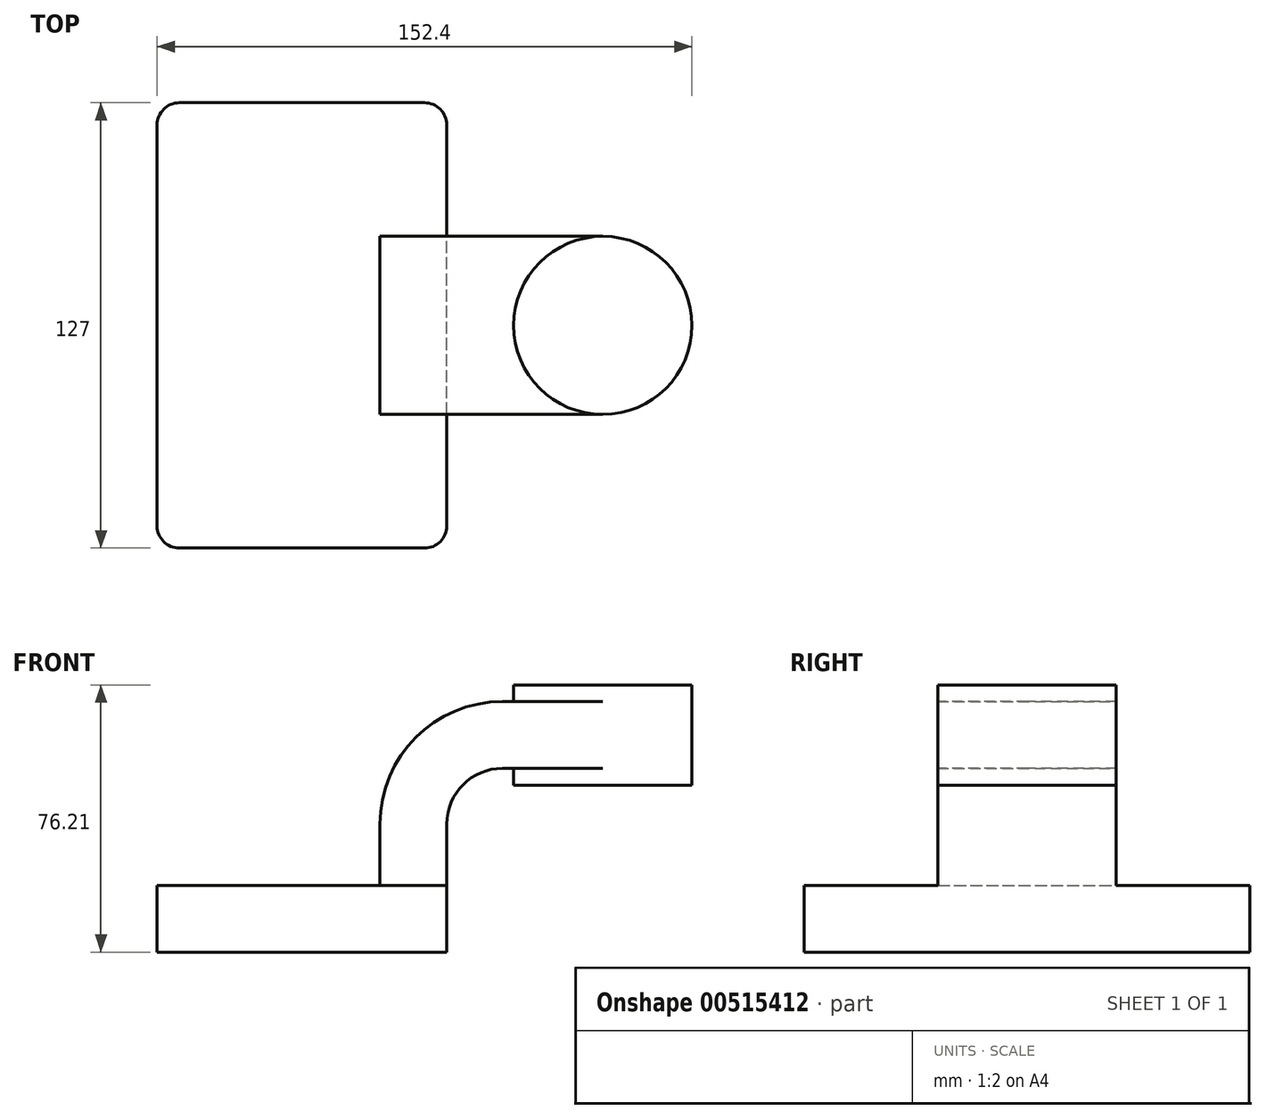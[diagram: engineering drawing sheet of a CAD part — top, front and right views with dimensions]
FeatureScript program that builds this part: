
annotation { "Feature Type Name" : "Feature", "Feature Type Description" : "" }
export const myFeature = defineFeature(function(context is Context, id is Id, definition is map)
    precondition{}
    {
        {
            var Q0;
            Q0=qCreatedBy(makeId("Front.planeOp"),FACE);
            var sketch = newSketch(context, id + "F0", { "sketchPlane" : qUnion([Q0])});
            skLineSegment(sketch, "E0.bottom", {"start": v(-41.28, 9.52) * mm, "end": v(41.28, 9.53) * mm});
            skLineSegment(sketch, "E0.top", {"start": v(-41.28, -9.53) * mm, "end": v(41.28, -9.53) * mm});
            skLineSegment(sketch, "E0.left", {"start": v(-41.28, 9.52) * mm, "end": v(-41.28, -9.53) * mm});
            skLineSegment(sketch, "E0.right", {"start": v(41.28, 9.53) * mm, "end": v(41.28, -9.52) * mm});
            skPoint(sketch, "E0.middle", {"position": v(0, 0) * mm});
            skLineSegment(sketch, "E1.bottom", {"start": v(60.32, 66.67) * mm, "end": v(111.12, 66.67) * mm});
            skLineSegment(sketch, "E1.top", {"start": v(60.32, 38.1) * mm, "end": v(111.12, 38.1) * mm});
            skLineSegment(sketch, "E1.left", {"start": v(60.32, 66.67) * mm, "end": v(60.32, 38.1) * mm});
            skLineSegment(sketch, "E1.right", {"start": v(111.12, 66.67) * mm, "end": v(111.12, 38.1) * mm});
            skPoint(sketch, "E1.middle", {"position": v(85.72, 52.39) * mm});
            skLineSegment(sketch, "E2", {"start": v(41.27, 9.53) * mm, "end": v(41.27, 27) * mm});
            skArc(sketch, "E3", {"start": v(41.27, 27) * mm, "mid": v(45.92, 38.23) * mm, "end": v(57.15, 42.88) * mm});
            skLineSegment(sketch, "E4", {"start": v(57.15, 42.88) * mm, "end": v(85.72, 42.88) * mm});
            skLineSegment(sketch, "E5.0", {"start": v(57.15, 61.93) * mm, "end": v(85.72, 61.93) * mm});
            skArc(sketch, "E5.1", {"start": v(22.23, 27) * mm, "mid": v(32.45, 51.7) * mm, "end": v(57.15, 61.93) * mm});
            skLineSegment(sketch, "E5.2", {"start": v(22.22, 9.53) * mm, "end": v(22.22, 27) * mm});
            skLineSegment(sketch, "E6", {"start": v(85.72, 42.88) * mm, "end": v(85.72, 61.93) * mm});
            skFitSpline(sketch, "E7", {"points": [v(-41.28, 9.53) * mm, v(57.15, 61.93) * mm], "startDerivative": vector(0.09, 88.97) * mm, "endDerivative": vector(162.63, -6.93) * mm});
            skLineSegment(sketch, "E8", {"start": v(85.72, 61.93) * mm, "end": v(85.72, 66.67) * mm});
            skLineSegment(sketch, "E9", {"start": v(85.72, 42.88) * mm, "end": v(85.72, 38.1) * mm});
            skSolve(sketch);
        }
        {
            var Q0;
            Q0=makeQuery(id+"F0.imprint","IMPRINT",FACE,{"disambiguationData":[TD([[makeQuery(id+"F0.imprint","IMPRINT",EDGE,{"derivedFrom":sQuery(id+"F0.wireOp",EDGE,"E0.top")}),1.0]])]});
            extrude(context, id + "F1", {"entities" : qUnion([Q0]), "endBound" : BoundingType.SYMMETRIC, "depth" : 127 * mm});
        }
        {
            var Q0;
            {var subQ1=sQuery(id+"F0.wireOp",EDGE,"E2");Q0=makeQuery(id+"F0.imprint","IMPRINT",FACE,{"disambiguationData":[TD([[makeQuery(id+"F0.imprint","IMPRINT",EDGE,{"derivedFrom":subQ1}),1.0]])]});}
            var Q1;
            {var subQ5=sQuery(id+"F0.wireOp",EDGE,"E6");Q1=makeQuery(id+"F0.imprint","IMPRINT",FACE,{"disambiguationData":[TD([[makeQuery(id+"F0.imprint","IMPRINT",EDGE,{"derivedFrom":subQ5}),1.0]])]});}
            extrude(context, id + "F2", {"entities" : qUnion([Q0, Q1]), "operationType" : NewBodyOperationType.ADD, "endBound" : BoundingType.SYMMETRIC, "depth" : 50.8 * mm});
        }
        {
            var Q0;
            Q0=makeQuery(id+"F0.imprint","IMPRINT",FACE,{"disambiguationData":[TD([[makeQuery(id+"F0.imprint","IMPRINT",EDGE,{"derivedFrom":sQuery(id+"F0.wireOp",EDGE,"E5.1")}),1.0]])]});
            extrude(context, id + "F3", {"entities" : qUnion([Q0]), "operationType" : NewBodyOperationType.ADD, "endBound" : BoundingType.SYMMETRIC, "depth" : 15.88 * mm});
        }
        {
            var Q0;
            {var subQ0=sQuery(id+"F0.wireOp",EDGE,"E1.right");Q0=makeQuery(id+"F0.imprint","IMPRINT",FACE,{"disambiguationData":[TD([[makeQuery(id+"F0.imprint","IMPRINT",EDGE,{"derivedFrom":subQ0}),-1.0]])]});}
            var Q1;
            Q1=sQuery(id+"F0.wireOp",EDGE,"E6");
            revolve(context, id + "F4", {"operationType" : NewBodyOperationType.ADD, "entities" : qUnion([Q0]), "axis" : qUnion([Q1]), "revolveType" : RevolveType.FULL});
        }
        {
            var Q0;
            Q0=makeQuery(id+"F1.opExtrude","CAP_EDGE",EDGE,{"disambiguationData":[OSD([sQuery(id+"F0.wireOp",EDGE,"E0.left")])],"isStart":true});
            var Q1;
            Q1=makeQuery(id+"F1.opExtrude","CAP_EDGE",EDGE,{"disambiguationData":[OSD([sQuery(id+"F0.wireOp",EDGE,"E0.right")])],"isStart":true});
            var Q2;
            Q2=makeQuery(id+"F1.opExtrude","CAP_EDGE",EDGE,{"disambiguationData":[OSD([sQuery(id+"F0.wireOp",EDGE,"E0.left")])],"isStart":false});
            var Q3;
            Q3=makeQuery(id+"F1.opExtrude","CAP_EDGE",EDGE,{"disambiguationData":[OSD([sQuery(id+"F0.wireOp",EDGE,"E0.right")])],"isStart":false});
            fillet(context, id + "F5", {"entities" : qUnion([Q0, Q1, Q2, Q3]), "radius" : 6.35 * mm, "tangentPropagation" : true, "allowEdgeOverflow" : false});
        }
    });
